# Revit family: Gymnasium-Eqpt_Volleyball_IPIbybison_Net-VB1000
name_source: partatom
category: Specialty Equipment
revit_build: Autodesk Revit 2018 (Build: 20170927_1515(x64)
units: mm (PartAtom-declared; Revit-internal decimal feet)

## family parameters
Always vertical = Yes
Cut with Voids When Loaded = No
OmniClass Number = 23.40.50.34.24
OmniClass Title = Nets
Part Type = Normal
Room Calculation Point = No
Round Connector Dimension = Use Diameter
Shared = No
Work Plane-Based = Yes

## types (2) — shared parameters
Assembly Code = E1090
Center to Center Posts = 37' - 0"
Default Elevation = 0' - 0"
Manufacturer = IPI by Bison
Manufacturer Fax = 800-638-0698
Manufacturer Website = https://ipibybison.com
Model = VB1000
Product Data = http://www.arcat.com
Revision = R0_2018-07
Sales Information = https://ipibybison.com
Standards Conformance = NCAA  ;  USVBA  ;  NFHS  ;  FIVB
URL = https://ipibybison.com
zero-valued in all types: Expected Lifespan (Years), Maintenance Schedule (Months), Warranty Duration (Years)

## per-type parameters (varying)
| type | Description |
| VB1000 | IPI by Bison Volleyball Net - VB1000NS Centerline as Specified |
| VB1000NS | IPI by Bison Volleyball Net - VB1000 Centerline as Specified |

## geometry (parser evidence)
native form markers: Sweep x3
no freeform markers — native parametric forms only
